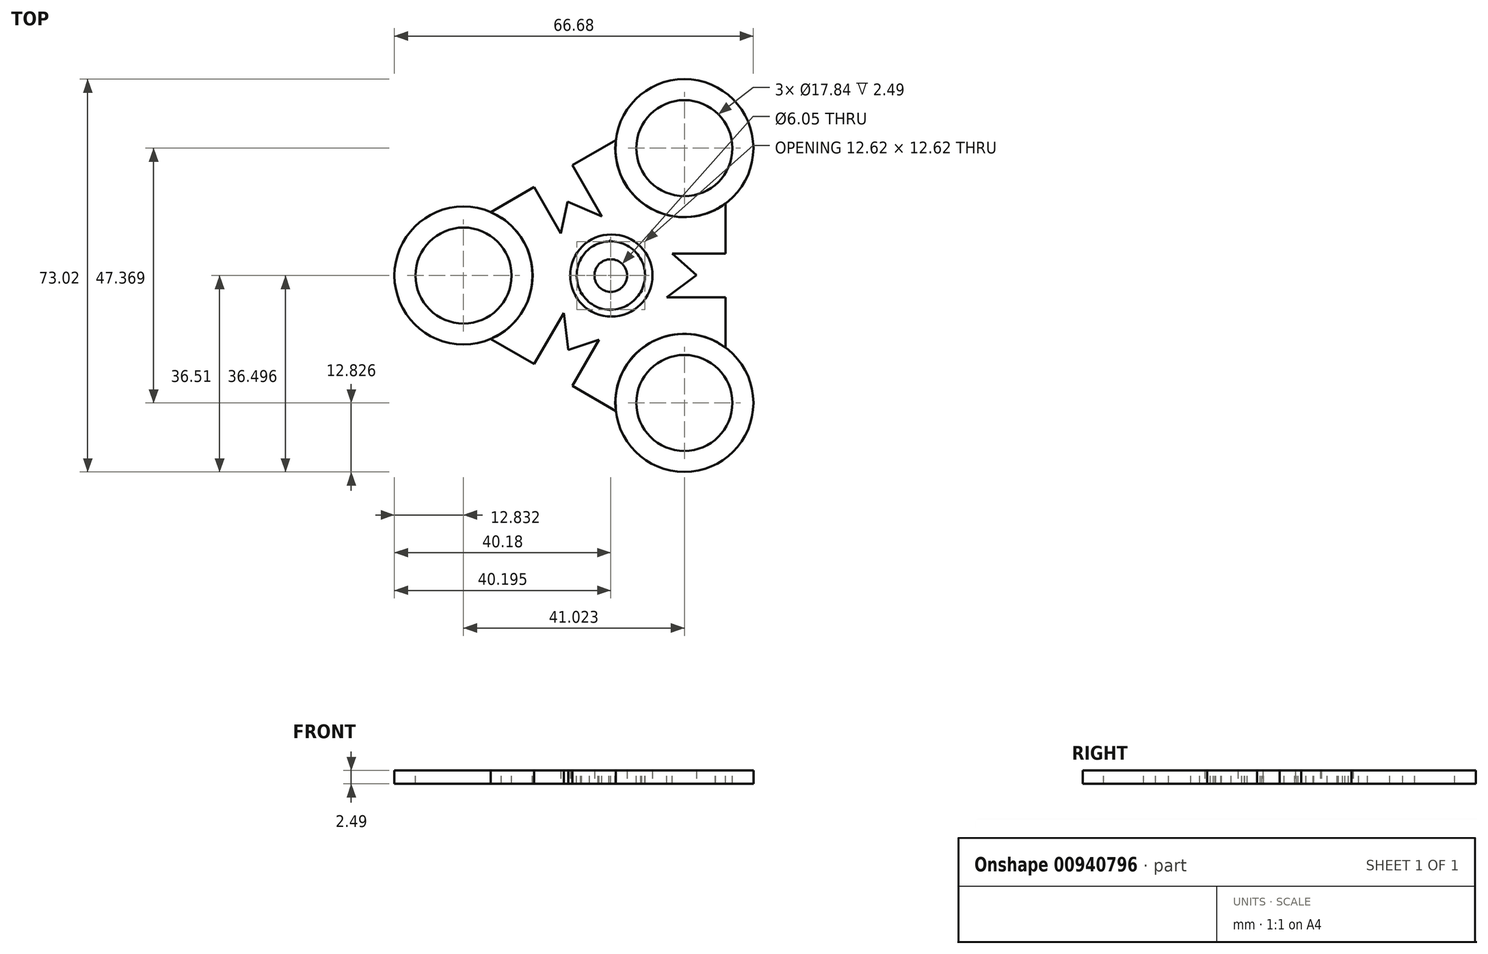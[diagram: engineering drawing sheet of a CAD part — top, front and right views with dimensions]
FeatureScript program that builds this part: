
annotation { "Feature Type Name" : "Feature", "Feature Type Description" : "" }
export const myFeature = defineFeature(function(context is Context, id is Id, definition is map)
    precondition{}
    {
        {
            var Q0;
            Q0=qCreatedBy(makeId("Top.planeOp"),FACE);
            var sketch = newSketch(context, id + "F0", { "sketchPlane" : qUnion([Q0])});
            skCircle(sketch, "E0", {"center": v(0, 0) * mm, "radius": 3.02 * mm});
            skCircle(sketch, "E1", {"center": v(0.11, 0) * mm, "radius": 7.63 * mm});
            skSolve(sketch);
        }
        {
            var Q0;
            Q0=makeQuery(id+"F0.imprint","IMPRINT",FACE,{"disambiguationData":[TD([[makeQuery(id+"F0.imprint","IMPRINT",EDGE,{"derivedFrom":sQuery(id+"F0.wireOp",EDGE,"E0")}),-1.0]])]});
            extrude(context, id + "F1", {"entities" : qUnion([Q0]), "depth" : 2.5 * mm, "offsetDistance" : 25.4 * mm});
        }
        {
            var Q0;
            Q0=makeQuery(id+"F1.opExtrude","CAP_FACE",FACE,{"disambiguationData":[OSD([sQuery(id+"F0.wireOp",EDGE,"E0"),sQuery(id+"F0.wireOp",EDGE,"E1")])],"isStart":false});
            var sketch = newSketch(context, id + "F2", { "sketchPlane" : qUnion([Q0])});
            skCircle(sketch, "E2", {"center": v(-27.35, 0) * mm, "radius": 8.92 * mm});
            skCircle(sketch, "E3", {"center": v(-27.35, 0) * mm, "radius": 12.83 * mm});
            skCircle(sketch, "E4.1.0", {"center": v(13.67, -23.68) * mm, "radius": 12.83 * mm});
            skCircle(sketch, "E4.1.1", {"center": v(13.67, -23.68) * mm, "radius": 8.92 * mm});
            skCircle(sketch, "E4.2.0", {"center": v(13.67, 23.68) * mm, "radius": 12.83 * mm});
            skCircle(sketch, "E4.2.1", {"center": v(13.67, 23.68) * mm, "radius": 8.92 * mm});
            skPoint(sketch, "E4.center", {"position": v(0, 0) * mm});
            skSolve(sketch);
        }
        {
            var Q0;
            Q0 = qSketchRegion(id + "F2", true);
            extrude(context, id + "F3", {"entities" : qUnion([Q0]), "oppositeDirection" : true, "depth" : 2.5 * mm, "offsetDistance" : 25.4 * mm});
        }
        {
            var Q0;
            Q0=makeQuery(id+"F3.opExtrude","CAP_FACE",FACE,{"disambiguationData":[OSD([sQuery(id+"F2.wireOp",EDGE,"E2"),sQuery(id+"F2.wireOp",EDGE,"E3")])],"isStart":true});
            var sketch = newSketch(context, id + "F4", { "sketchPlane" : qUnion([Q0])});
            skArc(sketch, "E5", {"start": v(-22.28, 11.78) * mm, "mid": v(-11.52, 7.53) * mm, "end": v(0, 6.46) * mm});
            skArc(sketch, "E6", {"start": v(0, -6.43) * mm, "mid": v(-11.52, -7.52) * mm, "end": v(-22.28, -11.78) * mm});
            skArc(sketch, "E7", {"start": v(-22.28, -11.78) * mm, "mid": v(-14.5, 0) * mm, "end": v(-22.28, 11.78) * mm});
            skArc(sketch, "E8", {"start": v(0, 6.46) * mm, "mid": v(-6.34, 0.02) * mm, "end": v(0, -6.43) * mm});
            skArc(sketch, "E9.1.0", {"start": v(5.57, 3.21) * mm, "mid": v(12.27, -6.22) * mm, "end": v(21.34, -13.4) * mm});
            skArc(sketch, "E9.1.1", {"start": v(21.34, -13.4) * mm, "mid": v(7.25, -12.56) * mm, "end": v(0.94, -25.19) * mm});
            skArc(sketch, "E9.1.2", {"start": v(0.94, -25.19) * mm, "mid": v(-0.76, -13.74) * mm, "end": v(-5.6, -3.23) * mm});
            skArc(sketch, "E9.1.3", {"start": v(-5.6, -3.23) * mm, "mid": v(3.15, -5.5) * mm, "end": v(5.57, 3.21) * mm});
            skArc(sketch, "E9.2.0", {"start": v(-5.57, 3.21) * mm, "mid": v(-0.75, 13.74) * mm, "end": v(0.94, 25.19) * mm});
            skArc(sketch, "E9.2.1", {"start": v(0.94, 25.19) * mm, "mid": v(7.25, 12.56) * mm, "end": v(21.34, 13.4) * mm});
            skArc(sketch, "E9.2.2", {"start": v(21.34, 13.4) * mm, "mid": v(12.28, 6.21) * mm, "end": v(5.6, -3.23) * mm});
            skArc(sketch, "E9.2.3", {"start": v(5.6, -3.23) * mm, "mid": v(3.18, 5.48) * mm, "end": v(-5.57, 3.21) * mm});
            skPoint(sketch, "E9.center", {"position": v(0, 0) * mm});
            skLineSegment(sketch, "E10", {"start": v(21.34, 13.4) * mm, "end": v(21.34, 4.1) * mm});
            skLineSegment(sketch, "E11", {"start": v(21.34, 4.1) * mm, "end": v(10.41, 4.1) * mm});
            skLineSegment(sketch, "E12", {"start": v(21.34, -13.4) * mm, "end": v(21.34, -4.08) * mm});
            skLineSegment(sketch, "E13", {"start": v(21.34, -4.08) * mm, "end": v(10.38, -4.08) * mm});
            skLineSegment(sketch, "E14.1.0", {"start": v(-7.14, 20.52) * mm, "end": v(-1.65, 11.03) * mm});
            skLineSegment(sketch, "E14.1.1", {"start": v(0.94, 25.19) * mm, "end": v(-7.14, 20.52) * mm});
            skLineSegment(sketch, "E14.1.2", {"start": v(-14.22, 16.44) * mm, "end": v(-8.75, 6.97) * mm});
            skLineSegment(sketch, "E14.1.3", {"start": v(-22.28, 11.78) * mm, "end": v(-14.22, 16.44) * mm});
            skLineSegment(sketch, "E14.2.0", {"start": v(-14.2, -16.44) * mm, "end": v(-8.72, -6.95) * mm});
            skLineSegment(sketch, "E14.2.1", {"start": v(-22.28, -11.78) * mm, "end": v(-14.2, -16.44) * mm});
            skLineSegment(sketch, "E14.2.2", {"start": v(-7.13, -20.53) * mm, "end": v(-1.66, -11.06) * mm});
            skLineSegment(sketch, "E14.2.3", {"start": v(0.94, -25.19) * mm, "end": v(-7.13, -20.53) * mm});
            skSolve(sketch);
        }
        {
            var Q0;
            Q0 = qSketchRegion(id + "F4", true);
            extrude(context, id + "F5", {"entities" : qUnion([Q0]), "oppositeDirection" : true, "depth" : 2.5 * mm, "offsetDistance" : 25.4 * mm});
        }
        {
            var Q0;
            Q0=makeQuery(id+"F5.opExtrude","SWEPT_EDGE",EDGE,{"disambiguationData":[OSD([sQuery(id+"F4.wireOp",EDGE,"E5"),sQuery(id+"F4.wireOp",EDGE,"E9.2.0")])]});
            fillet(context, id + "F6", {"entities" : qUnion([Q0]), "radius" : 13.75 * mm, "tangentPropagation" : true, "allowEdgeOverflow" : false});
        }
        {
            var Q0;
            Q0=makeQuery(id+"F5.opExtrude","SWEPT_EDGE",EDGE,{"disambiguationData":[OSD([sQuery(id+"F4.wireOp",EDGE,"E6"),sQuery(id+"F4.wireOp",EDGE,"E9.1.2")])]});
            fillet(context, id + "F7", {"entities" : qUnion([Q0]), "radius" : 13.74 * mm, "tangentPropagation" : true, "allowEdgeOverflow" : false});
        }
        {
            var Q0;
            Q0=makeQuery(id+"F5.opExtrude","SWEPT_EDGE",EDGE,{"disambiguationData":[OSD([sQuery(id+"F4.wireOp",EDGE,"E9.1.0"),sQuery(id+"F4.wireOp",EDGE,"E9.2.2")])]});
            fillet(context, id + "F8", {"entities" : qUnion([Q0]), "radius" : 13.74 * mm, "tangentPropagation" : true, "allowEdgeOverflow" : false});
        }
        {
            var Q0;
            Q0=makeQuery(id+"F5.opExtrude","CAP_FACE",FACE,{"disambiguationData":[OSD([sQuery(id+"F4.wireOp",EDGE,"E5"),sQuery(id+"F4.wireOp",EDGE,"E6"),sQuery(id+"F4.wireOp",EDGE,"E7"),sQuery(id+"F4.wireOp",EDGE,"E8"),sQuery(id+"F4.wireOp",EDGE,"E9.1.0"),sQuery(id+"F4.wireOp",EDGE,"E9.1.1"),sQuery(id+"F4.wireOp",EDGE,"E9.1.2"),sQuery(id+"F4.wireOp",EDGE,"E9.1.3"),sQuery(id+"F4.wireOp",EDGE,"E9.2.0"),sQuery(id+"F4.wireOp",EDGE,"E9.2.1"),sQuery(id+"F4.wireOp",EDGE,"E9.2.2"),sQuery(id+"F4.wireOp",EDGE,"E9.2.3"),sQuery(id+"F4.wireOp",EDGE,"E10"),sQuery(id+"F4.wireOp",EDGE,"E11"),sQuery(id+"F4.wireOp",EDGE,"E12"),sQuery(id+"F4.wireOp",EDGE,"E13"),sQuery(id+"F4.wireOp",EDGE,"E14.1.0"),sQuery(id+"F4.wireOp",EDGE,"E14.1.1"),sQuery(id+"F4.wireOp",EDGE,"E14.1.2"),sQuery(id+"F4.wireOp",EDGE,"E14.1.3"),sQuery(id+"F4.wireOp",EDGE,"E14.2.0"),sQuery(id+"F4.wireOp",EDGE,"E14.2.1"),sQuery(id+"F4.wireOp",EDGE,"E14.2.2"),sQuery(id+"F4.wireOp",EDGE,"E14.2.3")])],"isStart":false});
            var sketch = newSketch(context, id + "F9", { "sketchPlane" : qUnion([Q0])});
            skLineSegment(sketch, "E15", {"start": v(10.38, 4.08) * mm, "end": v(15.94, -0.09) * mm});
            skLineSegment(sketch, "E16", {"start": v(15.94, -0.09) * mm, "end": v(11.41, -4.1) * mm});
            skPoint(sketch, "E17.orphan", {"position": v(21.6, -0.09) * mm});
            skPoint(sketch, "E18.start.orphan", {"position": v(10.27, -0.09) * mm});
            skLineSegment(sketch, "E19.1.0", {"start": v(-8.72, 6.95) * mm, "end": v(-7.9, 13.84) * mm});
            skLineSegment(sketch, "E19.1.1", {"start": v(-7.9, 13.84) * mm, "end": v(-2.16, 11.93) * mm});
            skLineSegment(sketch, "E19.2.0", {"start": v(-1.65, -11.03) * mm, "end": v(-8.04, -13.76) * mm});
            skLineSegment(sketch, "E19.2.1", {"start": v(-8.04, -13.76) * mm, "end": v(-9.25, -7.84) * mm});
            skPoint(sketch, "E19.center", {"position": v(0, 0) * mm});
            skSolve(sketch);
        }
        {
            var Q0;
            Q0=makeQuery(id+"F9.imprint","IMPRINT",FACE,{"disambiguationData":[TD([[makeQuery(id+"F9.imprint","IMPRINT",EDGE,{"derivedFrom":sQuery(id+"F9.wireOp",EDGE,"E15")}),-1.0]])]});
            var Q1;
            Q1=makeQuery(id+"F9.imprint","IMPRINT",FACE,{"disambiguationData":[TD([[makeQuery(id+"F9.imprint","IMPRINT",EDGE,{"derivedFrom":sQuery(id+"F9.wireOp",EDGE,"E19.1.0")}),-1.0]])]});
            extrude(context, id + "F10", {"entities" : qUnion([Q0, Q1]), "operationType" : NewBodyOperationType.ADD, "oppositeDirection" : true, "depth" : 2.5 * mm, "offsetDistance" : 25.4 * mm});
        }
        {
            var Q0;
            {var subQ0=sQuery(id+"F9.wireOp",EDGE,"E19.2.0");Q0=makeQuery(id+"F9.imprint","IMPRINT",FACE,{"disambiguationData":[TD([[makeQuery(id+"F9.imprint","IMPRINT",EDGE,{"derivedFrom":subQ0}),-1.0]])]});}
            extrude(context, id + "F11", {"entities" : qUnion([Q0]), "operationType" : NewBodyOperationType.ADD, "oppositeDirection" : true, "depth" : 2.5 * mm, "offsetDistance" : 25.4 * mm});
        }
    });
